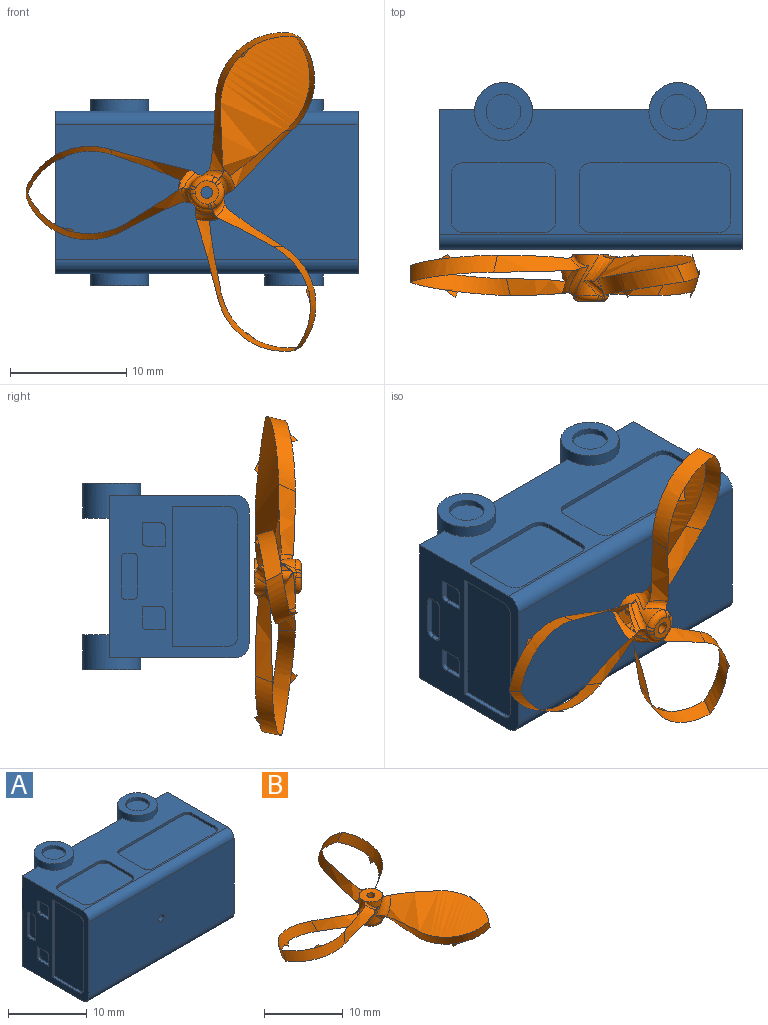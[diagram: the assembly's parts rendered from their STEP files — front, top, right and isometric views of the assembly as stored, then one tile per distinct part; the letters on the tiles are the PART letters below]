
ASSEMBLY  parts=2 mates=1
PART A: 105 faces, bbox 26x14.3x16 mm
  f0: cylinder r=2.5mm len=5mm, axis (0,0,-1), area 30.6mm2, adj f4,f9,f12,f102
  f1: cylinder r=2.5mm len=5mm, axis (0,0,-1), area 30.6mm2, adj f4,f9,f16,f100
  f2: plane 14x12mm, normal (1,0,0), area 107.9mm2, adj f4,f5,f8,f9,f88,f89,f90,f91
  f3: plane 14x12mm, normal (-1,0,0), area 87.2mm2, adj f4,f5,f8,f9,f58,f59,f60,f61
  f4: plane 26x10.8mm, normal (0,0,1), area 128.9mm2, adj f0,f1,f2,f3,f9,f40,f41,f42
  f5: plane 26x10.8mm, normal (0,0,-1), area 128.9mm2, adj f2,f3,f9,f10,f14,f22,f23,f24
  f6: cylinder r=1.5mm len=3mm, axis (0,0,-1), area 4.7mm2, adj f17,f20
  f7: cylinder r=1.5mm len=3mm, axis (0,0,-1), area 4.7mm2, adj f13,f18
  f8: plane 26x11.6mm, normal (0,-1,0), area 300.8mm2, adj f2,f3,f88,f89,f103
  f9: plane 26x14mm, normal (0,1,0), area 324.1mm2, adj f0,f1,f2,f3,f4,f5,f10,f14
  f10: cylinder r=2.5mm len=5mm, axis (0,0,-1), area 30.6mm2, adj f5,f9,f13,f101
  f11: cylinder r=1.5mm len=3mm, axis (0,0,-1), area 4.7mm2, adj f12,f19
  f12: plane 5x5mm, normal (0,0,1), area 12.6mm2, adj f0,f11
  f13: plane 5x5mm, normal (0,0,-1), area 12.6mm2, adj f7,f10
  f14: cylinder r=2.5mm len=5mm, axis (0,0,-1), area 30.6mm2, adj f5,f9,f17,f99
  f15: cylinder r=1.5mm len=3mm, axis (0,0,-1), area 4.7mm2, adj f16,f21
  f16: plane 5x5mm, normal (0,0,1), area 12.6mm2, adj f1,f15
  f17: plane 5x5mm, normal (0,0,-1), area 12.6mm2, adj f6,f14
  f18: plane 3x3mm, normal (0,0,-1), area 7.1mm2, adj f7
  f19: plane 3x3mm, normal (0,0,1), area 7.1mm2, adj f11
  f20: plane 3x3mm, normal (0,0,-1), area 7.1mm2, adj f6
  f21: plane 3x3mm, normal (0,0,1), area 7.1mm2, adj f15
  f22: plane 11x0.4mm, normal (0,1,0), area 4.4mm2, adj f5,f23,f29,f30
  f23: cylinder r=1mm len=1mm, axis (0,0,-1), area 0.6mm2, adj f5,f22,f24,f30
  f24: plane 4x0.4mm, normal (1,0,0), area 1.6mm2, adj f5,f23,f25,f30
  f25: cylinder r=1mm len=1mm, axis (0,0,-1), area 0.6mm2, adj f5,f24,f26,f30
  f26: plane 11x0.4mm, normal (0,-1,0), area 4.4mm2, adj f5,f25,f27,f30
  f27: cylinder r=1mm len=1mm, axis (0,0,-1), area 0.6mm2, adj f5,f26,f28,f30
  f28: plane 4x0.4mm, normal (-1,0,0), area 1.6mm2, adj f5,f27,f29,f30
  f29: cylinder r=1mm len=1mm, axis (0,0,-1), area 0.6mm2, adj f5,f22,f28,f30
  f30: plane 13x6mm, normal (0,0,-1), area 77.1mm2, adj f22,f23,f24,f25,f26,f27,f28,f29
  f31: plane 7x0.4mm, normal (0,1,0), area 2.8mm2, adj f5,f32,f38,f39
  f32: cylinder r=1mm len=1mm, axis (0,0,-1), area 0.6mm2, adj f5,f31,f33,f39
  f33: plane 4x0.4mm, normal (1,0,0), area 1.6mm2, adj f5,f32,f34,f39
  f34: cylinder r=1mm len=1mm, axis (0,0,-1), area 0.6mm2, adj f5,f33,f35,f39
  f35: plane 7x0.4mm, normal (0,-1,0), area 2.8mm2, adj f5,f34,f36,f39
  f36: cylinder r=1mm len=1mm, axis (0,0,-1), area 0.6mm2, adj f5,f35,f37,f39
  f37: plane 4x0.4mm, normal (-1,0,0), area 1.6mm2, adj f5,f36,f38,f39
  f38: cylinder r=1mm len=1mm, axis (0,0,-1), area 0.6mm2, adj f5,f31,f37,f39
  f39: plane 9x6mm, normal (0,0,-1), area 53.1mm2, adj f31,f32,f33,f34,f35,f36,f37,f38
  f40: plane 4x0.4mm, normal (1,0,0), area 1.6mm2, adj f4,f41,f47,f48
  f41: cylinder r=1mm len=1mm, axis (0,0,1), area 0.6mm2, adj f4,f40,f42,f48
  f42: plane 7x0.4mm, normal (0,1,0), area 2.8mm2, adj f4,f41,f43,f48
  f43: cylinder r=1mm len=1mm, axis (0,0,1), area 0.6mm2, adj f4,f42,f44,f48
  f44: plane 4x0.4mm, normal (-1,0,0), area 1.6mm2, adj f4,f43,f45,f48
  f45: cylinder r=1mm len=1mm, axis (0,0,1), area 0.6mm2, adj f4,f44,f46,f48
  f46: plane 7x0.4mm, normal (0,-1,0), area 2.8mm2, adj f4,f45,f47,f48
  f47: cylinder r=1mm len=1mm, axis (0,0,1), area 0.6mm2, adj f4,f40,f46,f48
  f48: plane 9x6mm, normal (0,0,1), area 53.1mm2, adj f40,f41,f42,f43,f44,f45,f46,f47
  f49: plane 11x0.4mm, normal (0,1,0), area 4.4mm2, adj f4,f50,f56,f57
  f50: cylinder r=1mm len=1mm, axis (0,0,1), area 0.6mm2, adj f4,f49,f51,f57
  f51: plane 4x0.4mm, normal (-1,0,0), area 1.6mm2, adj f4,f50,f52,f57
  f52: cylinder r=1mm len=1mm, axis (0,0,1), area 0.6mm2, adj f4,f51,f53,f57
  f53: plane 11x0.4mm, normal (0,-1,0), area 4.4mm2, adj f4,f52,f54,f57
  f54: cylinder r=1mm len=1mm, axis (0,0,1), area 0.6mm2, adj f4,f53,f55,f57
  f55: plane 4x0.4mm, normal (1,0,0), area 1.6mm2, adj f4,f54,f56,f57
  f56: cylinder r=1mm len=1mm, axis (0,0,1), area 0.6mm2, adj f4,f49,f55,f57
  f57: plane 13x6mm, normal (0,0,1), area 77.1mm2, adj f49,f50,f51,f52,f53,f54,f55,f56
  f58: plane 1.6x0.4mm, normal (0,1,0), area 0.6mm2, adj f3,f59,f63,f64
  f59: cylinder r=0.4mm len=0.4mm, axis (-1,0,0), area 0.3mm2, adj f3,f58,f60,f64
  f60: plane 1.6x0.4mm, normal (0,0,-1), area 0.6mm2, adj f3,f59,f61,f64
  f61: plane 1.6x0.4mm, normal (0,-1,0), area 0.6mm2, adj f3,f60,f62,f64
  f62: cylinder r=0.4mm len=0.4mm, axis (-1,0,0), area 0.3mm2, adj f3,f61,f63,f64
  f63: plane 1.6x0.4mm, normal (0,0,1), area 0.6mm2, adj f3,f58,f62,f64
  f64: plane 2x2mm, normal (-1,0,0), area 3.9mm2, adj f58,f59,f60,f61,f62,f63
  f65: plane 3.2x0.4mm, normal (0,1,0), area 1.3mm2, adj f3,f66,f72,f73
  f66: cylinder r=0.4mm len=0.4mm, axis (-1,0,0), area 0.3mm2, adj f3,f65,f67,f73
  f67: plane 0.6x0.4mm, normal (0,0,-1), area 0.2mm2, adj f3,f66,f68,f73
  f68: cylinder r=0.4mm len=0.4mm, axis (-1,0,0), area 0.3mm2, adj f3,f67,f69,f73
  f69: plane 3.2x0.4mm, normal (0,-1,0), area 1.3mm2, adj f3,f68,f70,f73
  f70: cylinder r=0.4mm len=0.4mm, axis (-1,0,0), area 0.3mm2, adj f3,f69,f71,f73
  f71: plane 0.6x0.4mm, normal (0,0,1), area 0.2mm2, adj f3,f70,f72,f73
  f72: cylinder r=0.4mm len=0.4mm, axis (-1,0,0), area 0.3mm2, adj f3,f65,f71,f73
  f73: plane 4x1.4mm, normal (-1,0,0), area 5.5mm2, adj f65,f66,f67,f68,f69,f70,f71,f72
  f74: plane 1.6x0.4mm, normal (0,1,0), area 0.6mm2, adj f3,f75,f79,f80
  f75: cylinder r=0.4mm len=0.4mm, axis (-1,0,0), area 0.3mm2, adj f3,f74,f76,f80
  f76: plane 1.6x0.4mm, normal (0,0,-1), area 0.6mm2, adj f3,f75,f77,f80
  f77: plane 1.6x0.4mm, normal (0,-1,0), area 0.6mm2, adj f3,f76,f78,f80
  f78: cylinder r=0.4mm len=0.4mm, axis (-1,0,0), area 0.3mm2, adj f3,f77,f79,f80
  f79: plane 1.6x0.4mm, normal (0,0,1), area 0.6mm2, adj f3,f74,f78,f80
  f80: plane 2x2mm, normal (-1,0,0), area 3.9mm2, adj f74,f75,f76,f77,f78,f79
  f81: plane 4.8x0.4mm, normal (0,0,1), area 1.9mm2, adj f3,f82,f86,f87
  f82: cylinder r=0.8mm len=0.8mm, axis (-1,0,0), area 0.5mm2, adj f3,f81,f83,f87
  f83: plane 10.4x0.4mm, normal (0,1,0), area 4.2mm2, adj f3,f82,f84,f87
  f84: cylinder r=0.8mm len=0.8mm, axis (-1,0,0), area 0.5mm2, adj f3,f83,f85,f87
  f85: plane 4.8x0.4mm, normal (0,0,-1), area 1.9mm2, adj f3,f84,f86,f87
  f86: plane 12x0.4mm, normal (0,-1,0), area 4.8mm2, adj f3,f81,f85,f87
  f87: plane 12x5.6mm, normal (-1,0,0), area 66.9mm2, adj f81,f82,f83,f84,f85,f86
  f88: cylinder r=1.2mm len=26mm, axis (1,0,0), area 49mm2, adj f2,f3,f5,f8
  f89: cylinder r=1.2mm len=26mm, axis (-1,0,0), area 49mm2, adj f2,f3,f4,f8
  f90: plane 10.4x0.4mm, normal (0,1,0), area 4.2mm2, adj f2,f91,f97,f98
  f91: cylinder r=0.8mm len=0.8mm, axis (1,0,0), area 0.5mm2, adj f2,f90,f92,f98
  f92: plane 3.4x0.4mm, normal (0,0,1), area 1.4mm2, adj f2,f91,f93,f98
  f93: cylinder r=0.8mm len=0.8mm, axis (1,0,0), area 0.5mm2, adj f2,f92,f94,f98
  f94: plane 10.4x0.4mm, normal (0,-1,0), area 4.2mm2, adj f2,f93,f95,f98
  f95: cylinder r=0.8mm len=0.8mm, axis (1,0,0), area 0.5mm2, adj f2,f94,f96,f98
  f96: plane 3.4x0.4mm, normal (0,0,-1), area 1.4mm2, adj f2,f95,f97,f98
  f97: cylinder r=0.8mm len=0.8mm, axis (1,0,0), area 0.5mm2, adj f2,f90,f96,f98
  f98: plane 12x5mm, normal (1,0,0), area 59.5mm2, adj f90,f91,f92,f93,f94,f95,f96,f97
  f99: plane 4.98x2.3mm, normal (0,0,1), area 8.8mm2, adj f9,f14
  f100: plane 4.98x2.3mm, normal (0,0,-1), area 8.8mm2, adj f1,f9
  f101: plane 4.98x2.3mm, normal (0,0,1), area 8.8mm2, adj f9,f10
  f102: plane 4.98x2.3mm, normal (0,0,-1), area 8.8mm2, adj f0,f9
  f103: cylinder r=0.5mm len=4mm, axis (0,-1,0), area 12.6mm2, adj f8,f104
  f104: plane 1x1mm, normal (0,-1,0), area 0.8mm2, adj f103
PART B: 42 faces, bbox 35.4x39x9.6 mm
  f0: cylinder r=1.5mm len=3.5mm, axis (0,0,-1), area 3.5mm2, adj f4,f8,f10,f17,f36,f39
  f1: cylinder r=1.5mm len=3.5mm, axis (0,0,-1), area 3.5mm2, adj f4,f15,f16,f23,f30,f40
  f2: cylinder r=0.5mm len=4mm, axis (0,0,-1), area 12.6mm2, adj f4,f5
  f3: cylinder r=1.5mm len=3.5mm, axis (0,0,-1), area 3.5mm2, adj f4,f11,f20,f22,f35,f41
  f4: plane 3.19x3.15mm, normal (0,0,1), area 6.3mm2, adj f0,f1,f2,f3,f8,f15,f20,f39
  f5: plane 2.01x2mm, normal (0,0,-1), area 2.4mm2, adj f2,f30,f31,f32,f33,f34,f35,f36
  f6: bspline ~8.75x2.26mm, area 8.9mm2, adj f8,f9,f10,f29
  f7: bspline ~10.77x9.49mm, area 11.3mm2, adj f8,f9,f11,f28,f41
  f8: bspline ~4.57x3.23mm, area 3.7mm2, adj f0,f4,f6,f7,f10,f41
  f9: bspline ~2.72x2.3mm, area 1.3mm2, adj f6,f7,f10,f11
  f10: bspline ~2.39x1.97mm, area 1.4mm2, adj f0,f6,f8,f9,f11,f37,f38
  f11: bspline ~3.57x2.39mm, area 2mm2, adj f3,f7,f9,f10,f37,f41
  f12: bspline ~8.46x5.12mm, area 8.9mm2, adj f13,f15,f16,f24
  f13: bspline ~2.72x2.03mm, area 1.3mm2, adj f12,f14,f16,f17
  f14: bspline ~12.69x5.56mm, area 11.3mm2, adj f13,f15,f17,f25,f39
  f15: bspline ~4.57x3.45mm, area 3.7mm2, adj f1,f4,f12,f14,f16,f39
  f16: bspline ~2.07x1.97mm, area 1.4mm2, adj f1,f12,f13,f15,f17,f32,f34
  f17: bspline ~3.57x1.98mm, area 2mm2, adj f0,f13,f14,f16,f34,f39
  f18: bspline ~8.01x5.9mm, area 8.9mm2, adj f20,f21,f22,f26
  f19: bspline ~13.1x3.75mm, area 11.3mm2, adj f20,f21,f23,f27,f40
  f20: bspline ~4.57x2.91mm, area 3.7mm2, adj f3,f4,f18,f19,f22,f40
  f21: bspline ~2.72x2.35mm, area 1.3mm2, adj f18,f19,f22,f23
  f22: bspline ~2.16x1.97mm, area 1.4mm2, adj f3,f18,f20,f21,f23,f31,f33
  f23: bspline ~3.57x2.32mm, area 2mm2, adj f1,f19,f21,f22,f31,f40
  f24: bspline ~12.21x11.79mm, area 16.9mm2, adj f12,f25
  f25: bspline ~9.98x9.77mm, area 14.3mm2, adj f14,f24
  f26: bspline ~12.03x10.87mm, area 16.9mm2, adj f18,f27
  f27: bspline ~10.2x10.08mm, area 14.3mm2, adj f19,f26
  f28: bspline ~10.11x9.59mm, area 14.3mm2, adj f7,f29
  f29: bspline ~13.18x10.51mm, area 16.9mm2, adj f6,f28
  f30: torus R=1mm, axis (0,0,1), area 1.6mm2, adj f1,f5,f31,f32
  f31: bspline ~0.97x0.67mm, area 0.2mm2, adj f5,f22,f23,f30,f33
  f32: bspline ~0.79x0.57mm, area 0.3mm2, adj f5,f16,f30,f34
  f33: bspline ~0.88x0.79mm, area 0.3mm2, adj f5,f22,f31,f35
  f34: bspline ~1.01x0.8mm, area 0.2mm2, adj f5,f16,f17,f32,f36
  f35: torus R=1mm, axis (0,0,1), area 1.6mm2, adj f3,f5,f33,f37
  f36: torus R=1mm, axis (0,0,1), area 1.6mm2, adj f0,f5,f34,f38
  f37: bspline ~0.97x0.95mm, area 0.2mm2, adj f5,f10,f11,f35,f38
  f38: bspline ~0.89x0.83mm, area 0.3mm2, adj f5,f10,f36,f37
  f39: bspline ~2.03x1.64mm, area 0.7mm2, adj f0,f4,f14,f15,f17
  f40: bspline ~2.29x1.39mm, area 0.7mm2, adj f1,f4,f19,f20,f23
  f41: bspline ~2.49x1.39mm, area 0.7mm2, adj f3,f4,f7,f8,f11
PLACE A t=(-2.07,-0.62,0.33)mm fixed
PLACE B rot(axis=(-1,0,0),90deg) t=(10.93,-4.12,0.33)mm
MATE fastened B.f2 <-> A.f103  axis (0,1,0) through (10.93,-1.12,0.33)mm
